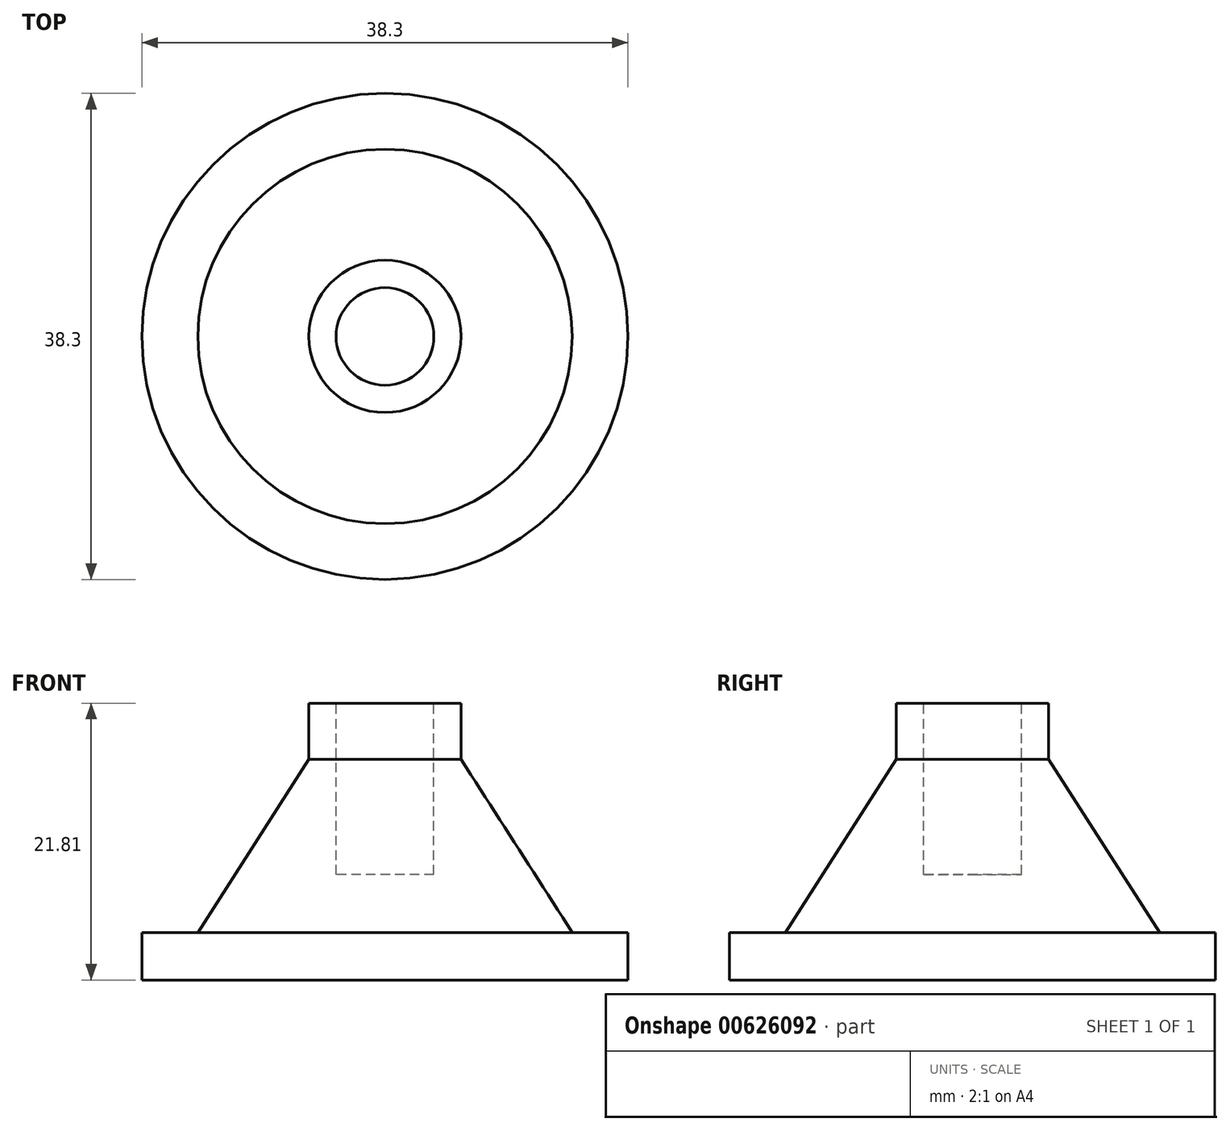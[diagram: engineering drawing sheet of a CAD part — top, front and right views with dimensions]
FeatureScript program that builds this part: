
annotation { "Feature Type Name" : "Feature", "Feature Type Description" : "" }
export const myFeature = defineFeature(function(context is Context, id is Id, definition is map)
    precondition{}
    {
        {
            var Q0;
            Q0=qCreatedBy(makeId("Front.planeOp"),FACE);
            var sketch = newSketch(context, id + "F0", { "sketchPlane" : qUnion([Q0])});
            skLineSegment(sketch, "E0", {"start": v(0, 0) * mm, "end": v(19.15, 0) * mm});
            skLineSegment(sketch, "E1", {"start": v(19.15, 0) * mm, "end": v(19.15, 3.74) * mm});
            skLineSegment(sketch, "E2", {"start": v(19.15, 3.74) * mm, "end": v(14.75, 3.74) * mm});
            skLineSegment(sketch, "E3", {"start": v(14.75, 3.74) * mm, "end": v(6, 17.37) * mm});
            skLineSegment(sketch, "E4", {"start": v(6, 17.37) * mm, "end": v(6, 21.81) * mm});
            skLineSegment(sketch, "E5", {"start": v(6, 21.81) * mm, "end": v(3.85, 21.81) * mm});
            skLineSegment(sketch, "E6", {"start": v(3.85, 21.81) * mm, "end": v(3.85, 8.31) * mm});
            skLineSegment(sketch, "E7", {"start": v(3.85, 8.31) * mm, "end": v(0, 8.31) * mm});
            skLineSegment(sketch, "E8", {"start": v(0, 8.31) * mm, "end": v(0, 0) * mm});
            skSolve(sketch);
        }
        {
            var Q0;
            Q0=makeQuery(id+"F0.imprint","IMPRINT",FACE,{"disambiguationData":[TD([[makeQuery(id+"F0.imprint","IMPRINT",EDGE,{"derivedFrom":sQuery(id+"F0.wireOp",EDGE,"E0")}),1.0]])]});
            var Q1;
            Q1=sQuery(id+"F0.wireOp",EDGE,"E8");
            revolve(context, id + "F1", {"surfaceOperationType" : NewSurfaceOperationType.NEW, "entities" : qUnion([Q0]), "axis" : qUnion([Q1]), "revolveType" : RevolveType.FULL});
        }
    });
